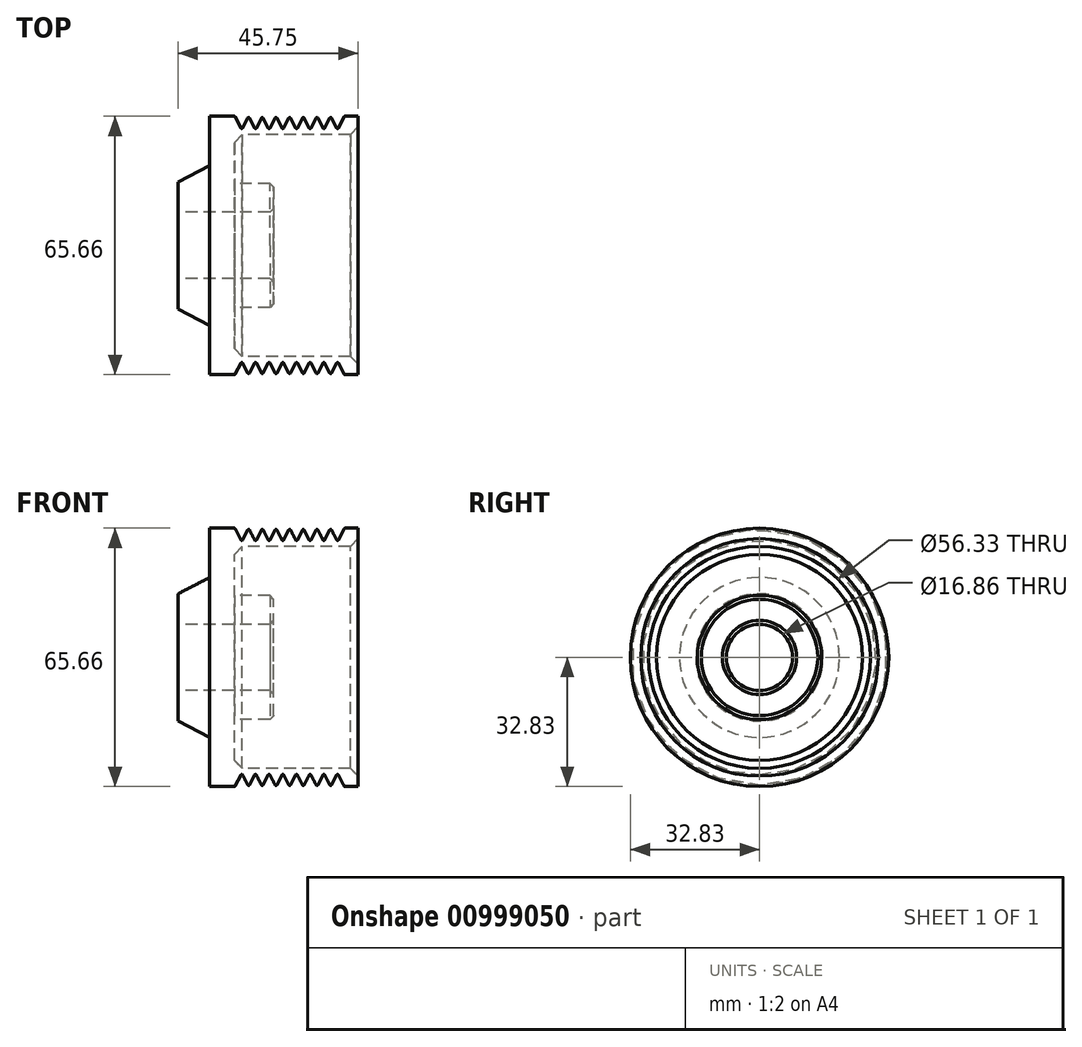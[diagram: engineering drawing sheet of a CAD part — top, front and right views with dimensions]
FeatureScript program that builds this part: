
annotation { "Feature Type Name" : "Feature", "Feature Type Description" : "" }
export const myFeature = defineFeature(function(context is Context, id is Id, definition is map)
    precondition{}
    {
        {
            var Q0;
            Q0=qCreatedBy(makeId("Front.planeOp"),FACE);
            var sketch = newSketch(context, id + "F0", { "sketchPlane" : qUnion([Q0])});
            skLineSegment(sketch, "E0", {"start": v(-38.13, 8.43) * mm, "end": v(-38.13, 16.18) * mm});
            skLineSegment(sketch, "E1", {"start": v(-38.13, 16.18) * mm, "end": v(-30.08, 20.34) * mm});
            skLineSegment(sketch, "E2", {"start": v(-30.08, 20.34) * mm, "end": v(-30.08, 32.83) * mm});
            skLineSegment(sketch, "E3", {"start": v(-13.83, 8.43) * mm, "end": v(-38.13, 8.43) * mm});
            skLineSegment(sketch, "E4", {"start": v(-45.5, 0) * mm, "end": v(-6.35, 0) * mm, "construction": true});
            skLineSegment(sketch, "E5", {"start": v(-23.83, 28.16) * mm, "end": v(-23.83, 15.79) * mm});
            skLineSegment(sketch, "E6", {"start": v(-23.83, 15.79) * mm, "end": v(-13.83, 15.8) * mm});
            skLineSegment(sketch, "E7", {"start": v(-13.83, 15.8) * mm, "end": v(-13.83, 8.43) * mm});
            skLineSegment(sketch, "E8", {"start": v(-30.08, 32.83) * mm, "end": v(-30.08, 32.83) * mm});
            skLineSegment(sketch, "E9", {"start": v(-30.08, 32.83) * mm, "end": v(7.62, 32.83) * mm});
            skLineSegment(sketch, "E10", {"start": v(7.62, 32.83) * mm, "end": v(7.62, 28.17) * mm});
            skLineSegment(sketch, "E11", {"start": v(7.62, 28.17) * mm, "end": v(-23.83, 28.16) * mm});
            skSolve(sketch);
        }
        {
            var Q0;
            Q0=qSketchRegion(id+"F0",true);
            var Q1;
            Q1=sQuery(id+"F0.wireOp",EDGE,"E4");
            revolve(context, id + "F1", {"surfaceOperationType" : NewSurfaceOperationType.NEW, "entities" : qUnion([Q0]), "axis" : qUnion([Q1]), "revolveType" : RevolveType.FULL});
        }
        {
            var Q0;
            Q0=qCreatedBy(makeId("Front.planeOp"),FACE);
            var sketch = newSketch(context, id + "F2", { "sketchPlane" : qUnion([Q0])});
            skLineSegment(sketch, "E12", {"start": v(-30.08, 42.61) * mm, "end": v(-30.08, 2.77) * mm, "construction": true});
            skLineSegment(sketch, "E13", {"start": v(-23.7, 41.1) * mm, "end": v(-23.7, 5.8) * mm, "construction": true});
            skLineSegment(sketch, "E14", {"start": v(-23.7, 32.83) * mm, "end": v(-21.97, 29.43) * mm});
            skLineSegment(sketch, "E15", {"start": v(-21.97, 29.43) * mm, "end": v(-20.23, 32.83) * mm});
            skLineSegment(sketch, "E16", {"start": v(-20.23, 32.83) * mm, "end": v(-23.7, 32.83) * mm});
            skLineSegment(sketch, "E17", {"start": v(-20.23, 32.83) * mm, "end": v(-18.5, 29.43) * mm});
            skLineSegment(sketch, "E18", {"start": v(-18.5, 29.43) * mm, "end": v(-16.75, 32.83) * mm});
            skLineSegment(sketch, "E19", {"start": v(-16.75, 32.83) * mm, "end": v(-15.02, 29.43) * mm});
            skLineSegment(sketch, "E20", {"start": v(-15.02, 29.43) * mm, "end": v(-13.28, 32.83) * mm});
            skLineSegment(sketch, "E21", {"start": v(-6.33, 32.83) * mm, "end": v(-4.6, 29.43) * mm});
            skLineSegment(sketch, "E22", {"start": v(4.1, 32.83) * mm, "end": v(0.62, 32.83) * mm});
            skLineSegment(sketch, "E23", {"start": v(0.62, 32.83) * mm, "end": v(-2.85, 32.83) * mm});
            skLineSegment(sketch, "E24", {"start": v(-2.85, 32.83) * mm, "end": v(-6.33, 32.83) * mm});
            skLineSegment(sketch, "E25", {"start": v(-6.33, 32.83) * mm, "end": v(-9.8, 32.83) * mm});
            skLineSegment(sketch, "E26", {"start": v(-9.8, 32.83) * mm, "end": v(-13.28, 32.83) * mm});
            skLineSegment(sketch, "E27", {"start": v(-13.28, 32.83) * mm, "end": v(-16.75, 32.83) * mm});
            skLineSegment(sketch, "E28", {"start": v(-16.75, 32.83) * mm, "end": v(-20.23, 32.83) * mm});
            skLineSegment(sketch, "E29", {"start": v(-13.28, 32.83) * mm, "end": v(-11.54, 29.43) * mm});
            skLineSegment(sketch, "E30", {"start": v(-11.54, 29.43) * mm, "end": v(-9.8, 32.83) * mm});
            skLineSegment(sketch, "E31", {"start": v(-9.8, 32.83) * mm, "end": v(-8.07, 29.43) * mm});
            skLineSegment(sketch, "E32", {"start": v(-8.07, 29.43) * mm, "end": v(-6.33, 32.83) * mm});
            skLineSegment(sketch, "E33", {"start": v(-2.85, 32.83) * mm, "end": v(-4.6, 29.43) * mm});
            skLineSegment(sketch, "E34", {"start": v(-2.85, 32.83) * mm, "end": v(-1.12, 29.43) * mm});
            skLineSegment(sketch, "E35", {"start": v(-1.12, 29.43) * mm, "end": v(0.62, 32.83) * mm});
            skLineSegment(sketch, "E36", {"start": v(0.62, 32.83) * mm, "end": v(2.36, 29.43) * mm});
            skLineSegment(sketch, "E37", {"start": v(2.36, 29.43) * mm, "end": v(4.1, 32.83) * mm});
            skSolve(sketch);
        }
        {
            var Q0;
            Q0=qSketchRegion(id+"F2",true);
            var Q1;
            Q1=sQuery(id+"F0.wireOp",EDGE,"E4");
            revolve(context, id + "F3", {"operationType" : NewBodyOperationType.REMOVE, "surfaceOperationType" : NewSurfaceOperationType.NEW, "entities" : qUnion([Q0]), "axis" : qUnion([Q1]), "revolveType" : RevolveType.FULL, "oppositeDirection" : true});
        }
        {
            var Q0;
            Q0=makeQuery(id+"F1.opRevolve","SWEPT_FACE",FACE,{"disambiguationData":[OSD([sQuery(id+"F0.wireOp",EDGE,"E11")])]});
            chamfer(context, id + "F4", {"entities" : qUnion([Q0]), "width" : 2 * mm});
        }
        {
            var Q0;
            Q0=makeQuery(id+"F1.opRevolve","SWEPT_FACE",FACE,{"disambiguationData":[OSD([sQuery(id+"F0.wireOp",EDGE,"E7")])]});
            chamfer(context, id + "F5", {"entities" : qUnion([Q0]), "width" : 1 * mm, "tangentPropagation" : true});
        }
        {
            var Q0;
            Q0=makeQuery(id+"F3.boolean.opBoolean","COPY",FACE,{"derivedFrom":makeQuery(id+"F3.opRevolve","SWEPT_FACE",FACE,{"disambiguationData":[OSD([sQuery(id+"F2.wireOp",EDGE,"E17")])]})});
            var Q1;
            Q1=makeQuery(id+"F3.boolean.opBoolean","COPY",FACE,{"derivedFrom":makeQuery(id+"F3.opRevolve","SWEPT_FACE",FACE,{"disambiguationData":[OSD([sQuery(id+"F2.wireOp",EDGE,"E14")])]})});
            var Q2;
            Q2=makeQuery(id+"F3.boolean.opBoolean","COPY",FACE,{"derivedFrom":makeQuery(id+"F3.opRevolve","SWEPT_FACE",FACE,{"disambiguationData":[OSD([sQuery(id+"F2.wireOp",EDGE,"E18")])]})});
            var Q3;
            Q3=makeQuery(id+"F3.boolean.opBoolean","COPY",FACE,{"derivedFrom":makeQuery(id+"F3.opRevolve","SWEPT_FACE",FACE,{"disambiguationData":[OSD([sQuery(id+"F2.wireOp",EDGE,"E19")])]})});
            var Q4;
            Q4=makeQuery(id+"F3.boolean.opBoolean","COPY",FACE,{"derivedFrom":makeQuery(id+"F3.opRevolve","SWEPT_FACE",FACE,{"disambiguationData":[OSD([sQuery(id+"F2.wireOp",EDGE,"E20")])]})});
            var Q5;
            Q5=makeQuery(id+"F3.boolean.opBoolean","COPY",FACE,{"derivedFrom":makeQuery(id+"F3.opRevolve","SWEPT_FACE",FACE,{"disambiguationData":[OSD([sQuery(id+"F2.wireOp",EDGE,"E29")])]})});
            var Q6;
            Q6=makeQuery(id+"F3.boolean.opBoolean","COPY",FACE,{"derivedFrom":makeQuery(id+"F3.opRevolve","SWEPT_FACE",FACE,{"disambiguationData":[OSD([sQuery(id+"F2.wireOp",EDGE,"E30")])]})});
            var Q7;
            Q7=makeQuery(id+"F3.boolean.opBoolean","COPY",FACE,{"derivedFrom":makeQuery(id+"F3.opRevolve","SWEPT_FACE",FACE,{"disambiguationData":[OSD([sQuery(id+"F2.wireOp",EDGE,"E31")])]})});
            var Q8;
            Q8=makeQuery(id+"F3.boolean.opBoolean","COPY",FACE,{"derivedFrom":makeQuery(id+"F3.opRevolve","SWEPT_FACE",FACE,{"disambiguationData":[OSD([sQuery(id+"F2.wireOp",EDGE,"E32")])]})});
            var Q9;
            Q9=makeQuery(id+"F3.boolean.opBoolean","COPY",FACE,{"derivedFrom":makeQuery(id+"F3.opRevolve","SWEPT_FACE",FACE,{"disambiguationData":[OSD([sQuery(id+"F2.wireOp",EDGE,"E21")])]})});
            var Q10;
            Q10=makeQuery(id+"F3.boolean.opBoolean","COPY",FACE,{"derivedFrom":makeQuery(id+"F3.opRevolve","SWEPT_FACE",FACE,{"disambiguationData":[OSD([sQuery(id+"F2.wireOp",EDGE,"E33")])]})});
            var Q11;
            Q11=makeQuery(id+"F3.boolean.opBoolean","COPY",FACE,{"derivedFrom":makeQuery(id+"F3.opRevolve","SWEPT_FACE",FACE,{"disambiguationData":[OSD([sQuery(id+"F2.wireOp",EDGE,"E34")])]})});
            var Q12;
            Q12=makeQuery(id+"F3.boolean.opBoolean","COPY",FACE,{"derivedFrom":makeQuery(id+"F3.opRevolve","SWEPT_FACE",FACE,{"disambiguationData":[OSD([sQuery(id+"F2.wireOp",EDGE,"E35")])]})});
            var Q13;
            Q13=makeQuery(id+"F3.boolean.opBoolean","COPY",FACE,{"derivedFrom":makeQuery(id+"F3.opRevolve","SWEPT_FACE",FACE,{"disambiguationData":[OSD([sQuery(id+"F2.wireOp",EDGE,"E36")])]})});
            var Q14;
            Q14=makeQuery(id+"F3.boolean.opBoolean","COPY",FACE,{"derivedFrom":makeQuery(id+"F3.opRevolve","SWEPT_FACE",FACE,{"disambiguationData":[OSD([sQuery(id+"F2.wireOp",EDGE,"E37")])]})});
            fillet(context, id + "F6", {"entities" : qUnion([Q0, Q1, Q2, Q3, Q4, Q5, Q6, Q7, Q8, Q9, Q10, Q11, Q12, Q13, Q14]), "radius" : .25 * mm, "tangentPropagation" : true, "allowEdgeOverflow" : false});
        }
    });
